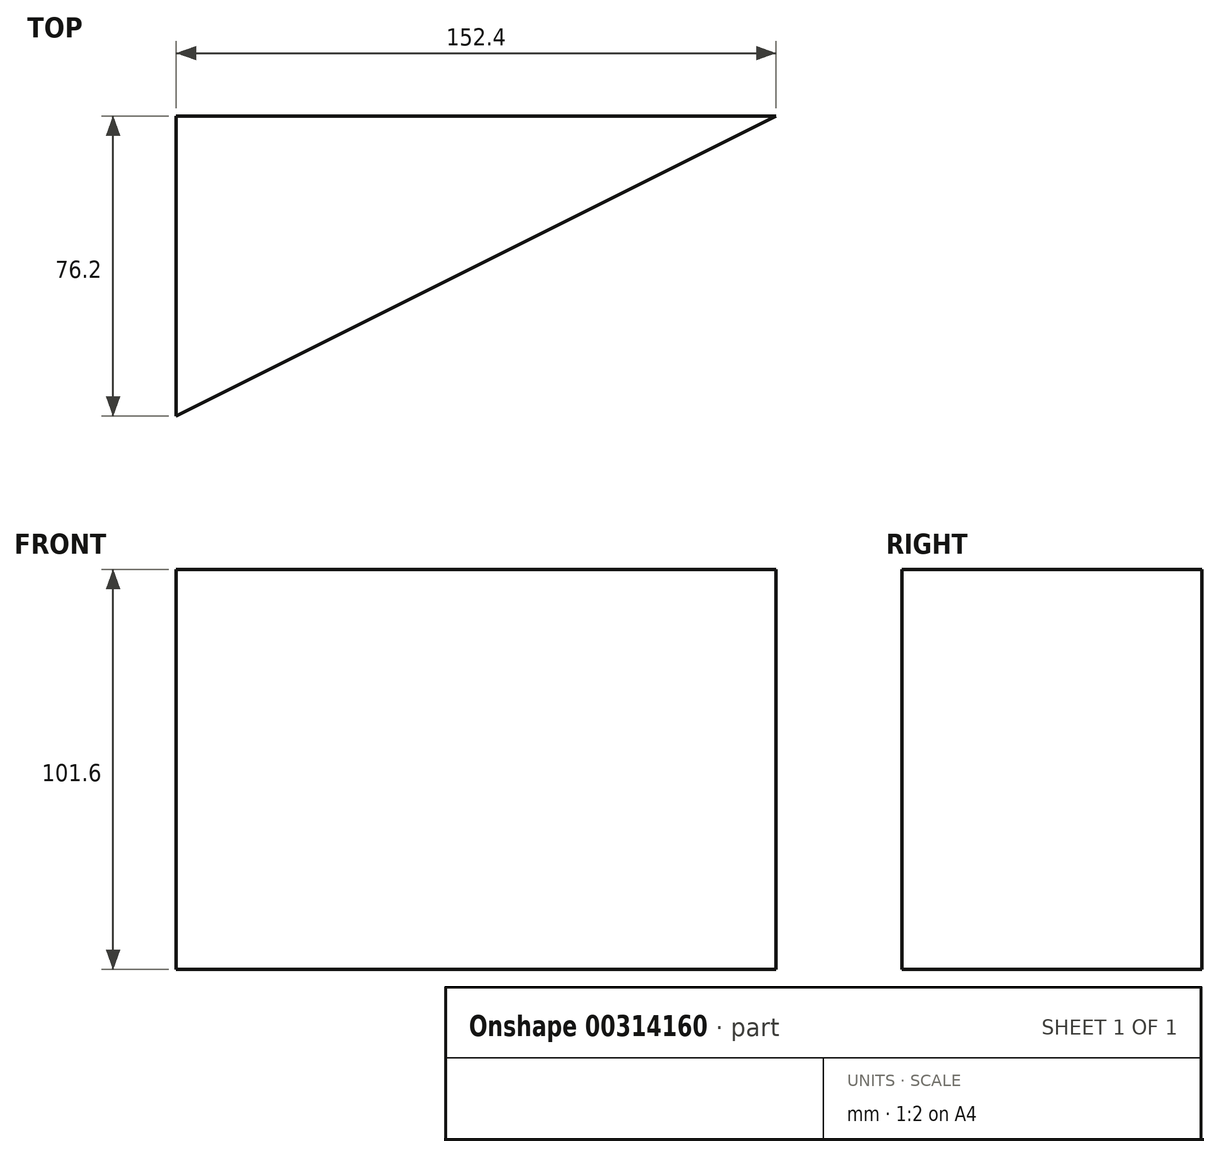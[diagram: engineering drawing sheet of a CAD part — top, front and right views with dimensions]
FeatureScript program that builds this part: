
annotation { "Feature Type Name" : "Feature", "Feature Type Description" : "" }
export const myFeature = defineFeature(function(context is Context, id is Id, definition is map)
    precondition{}
    {
        {
            var Q0;
            Q0=qCreatedBy(makeId("Top.planeOp"),FACE);
            var sketch = newSketch(context, id + "F0", { "sketchPlane" : qUnion([Q0])});
            skLineSegment(sketch, "E0.bottom", {"start": v(0, 0) * mm, "end": v(152.4, 0) * mm});
            skLineSegment(sketch, "E0.top", {"start": v(0, -76.2) * mm, "end": v(152.4, -76.2) * mm});
            skLineSegment(sketch, "E0.left", {"start": v(0, 0) * mm, "end": v(0, -76.2) * mm});
            skLineSegment(sketch, "E0.right", {"start": v(152.4, 0) * mm, "end": v(152.4, -76.2) * mm});
            skLineSegment(sketch, "E1", {"start": v(0, -76.2) * mm, "end": v(152.4, 0) * mm});
            skSolve(sketch);
        }
        {
            var Q0;
            Q0=makeQuery(id+"F0.imprint","IMPRINT",FACE,{"disambiguationData":[TD([[makeQuery(id+"F0.imprint","IMPRINT",EDGE,{"derivedFrom":sQuery(id+"F0.wireOp",EDGE,"E0.bottom")}),-1.0]])]});
            extrude(context, id + "F1", {"entities" : qUnion([Q0]), "depth" : 101.6 * mm});
        }
    });
